# Revit family: QF_MACON_CB91C-G-N
name_source: partatom
category: Equipamento especial
units: mm (PartAtom-declared; Revit-internal decimal feet)

## family parameters
Com base no plano de trabalho = Não
Compartilhado = Não
Corte com vazios quando carregada = Não
Cota do conector redondo = Utilizar diâmetro
Número OmniClass = 23.40.40.14.17.11
Ponto de cálculo do ambiente = Não
Sempre na vertical = Sim
Tipo de parte = Normal
Título OmniClass = Cookers, Ovens, Stoves

## types (2) — shared parameters
Depth = 972,00 mm
Fabricante = MACOM
Gas Connection Height = 62,00 mm
Gas Pressure = 0,0 bar
Gas Size = 1"
Height = 351,00 mm
Show Clearances = Sim
URL = https://www.acosmacom.com.br
Volume = 0,15 m³
Weight = 0,00 kg
Width = 450,00 mm

## per-type parameters (varying)
| type | Descrição | Gas Consumption GLP | Gas Consumption GN | Gas Input GLP | Gas Input GN |
| CB91C-G | CHAR BROILER A GAS GLP 900HP MACOM - 450X972X265MM | 1,03 Kg/h | 0,0 m³/h | 46854 Btu/h |  |
| CB91C-N | CHAR BROILER A GAS NATURAL  900HP MACOM - 450X972X265MM |  | 1,2 m³/h | 0 Btu/h | 11808 Kcal/h |

note: column(s) folded — value = type name in every type: Modelo

## geometry (parser evidence)
native form markers: Sweep x6
no freeform markers — native parametric forms only
